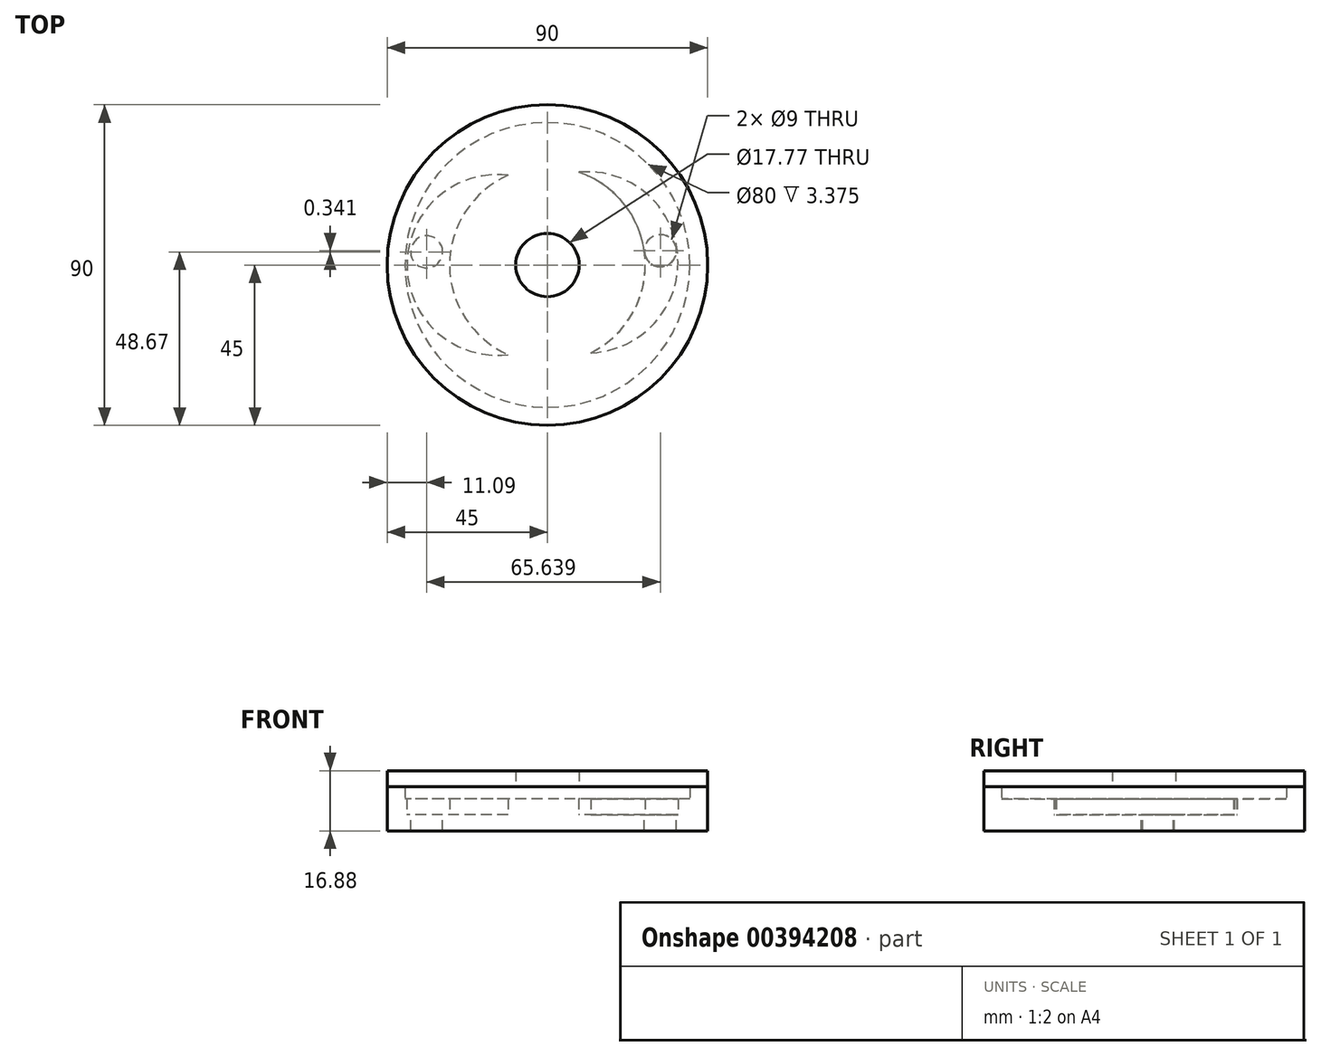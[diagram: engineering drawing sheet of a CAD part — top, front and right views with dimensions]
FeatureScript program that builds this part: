
annotation { "Feature Type Name" : "Feature", "Feature Type Description" : "" }
export const myFeature = defineFeature(function(context is Context, id is Id, definition is map)
    precondition{}
    {
        {
            var Q0;
            Q0=qCreatedBy(makeId("Top.planeOp"),FACE);
            var sketch = newSketch(context, id + "F0", { "sketchPlane" : qUnion([Q0])});
            skCircle(sketch, "E0", {"center": v(0, 0) * mm, "radius": 40 * mm});
            skCircle(sketch, "E1", {"center": v(0, 0) * mm, "radius": 45 * mm});
            skCircle(sketch, "E2", {"center": v(0, 0) * mm, "radius": 5 * mm});
            skSolve(sketch);
        }
        {
            var Q0;
            Q0=makeQuery(id+"F0.imprint","IMPRINT",FACE,{"disambiguationData":[TD([[makeQuery(id+"F0.imprint","IMPRINT",EDGE,{"derivedFrom":sQuery(id+"F0.wireOp",EDGE,"E0")}),1.0]])]});
            var Q1;
            Q1=makeQuery(id+"F0.imprint","IMPRINT",FACE,{"disambiguationData":[TD([[makeQuery(id+"F0.imprint","IMPRINT",EDGE,{"derivedFrom":sQuery(id+"F0.wireOp",EDGE,"E2")}),1.0]])]});
            extrude(context, id + "F1", {"entities" : qUnion([Q0, Q1]), "depth" : (2 * 9 / 4) * mm});
        }
        {
            var Q0;
            Q0=makeQuery(id+"F0.imprint","IMPRINT",FACE,{"disambiguationData":[TD([[makeQuery(id+"F0.imprint","IMPRINT",EDGE,{"derivedFrom":sQuery(id+"F0.wireOp",EDGE,"E0")}),-1.0]])]});
            extrude(context, id + "F2", {"entities" : qUnion([Q0]), "operationType" : NewBodyOperationType.ADD, "depth" : (3.5 * 9 / 4) * mm});
        }
        {
            var Q0;
            Q0=qCreatedBy(makeId("Top.planeOp"),FACE);
            var sketch = newSketch(context, id + "F3", { "sketchPlane" : qUnion([Q0])});
            skCircle(sketch, "E3", {"center": v(0, 0) * mm, "radius": 27.48 * mm});
            skCircle(sketch, "E4", {"center": v(-14.08, 0) * mm, "radius": 25.35 * mm});
            skCircle(sketch, "E5", {"center": v(11.25, 0.76) * mm, "radius": 25.4 * mm});
            skSolve(sketch);
        }
        {
            var Q0;
            {var subQ0=sQuery(id+"F3.wireOp",EDGE,"E5");var subQ1=sQuery(id+"F3.wireOp",EDGE,"E3");var subQ2=makeQuery(id+"F3.imprint","INTERSECT",VERTEX,{"disambiguationData":[OD(0.0)],"derivedFrom":[subQ1,subQ0]});Q0=makeQuery(id+"F3.imprint","IMPRINT",FACE,{"disambiguationData":[TD([[makeQuery(id+"F3.imprint","IMPRINT",EDGE,{"disambiguationData":[TD([[subQ2,1.0]])],"derivedFrom":subQ1}),-1.0]])]});}
            var Q1;
            {var subQ0=sQuery(id+"F3.wireOp",EDGE,"E4");var subQ1=sQuery(id+"F3.wireOp",EDGE,"E3");var subQ2=makeQuery(id+"F3.imprint","INTERSECT",VERTEX,{"disambiguationData":[OD(0.0)],"derivedFrom":[subQ1,subQ0]});Q1=makeQuery(id+"F3.imprint","IMPRINT",FACE,{"disambiguationData":[TD([[makeQuery(id+"F3.imprint","IMPRINT",EDGE,{"disambiguationData":[TD([[subQ2,-1.0]])],"derivedFrom":subQ1}),-1.0]])]});}
            var Q2;
            Q2=sQuery(id+"FPR7zcq1sT2BLRO_1.wireOp",EDGE,"gdkzTtUh-GniQ-s6fz-oA94-rAv7j2Bywu3O");
            extrude(context, id + "F4", {"entities" : qUnion([Q0, Q1]), "operationType" : NewBodyOperationType.REMOVE, "surfaceEntities" : qUnion([Q2]), "depth" : (2.5 * 9 / 4) * mm});
        }
        {
            var Q0;
            Q0=qCreatedBy(makeId("Top.planeOp"),FACE);
            var sketch = newSketch(context, id + "F5", { "sketchPlane" : qUnion([Q0])});
            skCircle(sketch, "E6", {"center": v(0, 0) * mm, "radius": 45 * mm});
            skCircle(sketch, "E7", {"center": v(-33.91, 3.67) * mm, "radius": 4.5 * mm});
            skCircle(sketch, "E8", {"center": v(31.73, 4.01) * mm, "radius": 4.5 * mm});
            skSolve(sketch);
        }
        {
            var Q0;
            Q0=makeQuery(id+"F5.imprint","IMPRINT",FACE,{"disambiguationData":[TD([[makeQuery(id+"F5.imprint","IMPRINT",EDGE,{"derivedFrom":sQuery(id+"F5.wireOp",EDGE,"E6")}),1.0]])]});
            extrude(context, id + "F6", {"entities" : qUnion([Q0]), "operationType" : NewBodyOperationType.ADD, "oppositeDirection" : true, "depth" : (2 * 9 / 4) * mm});
        }
        {
            var Q0;
            Q0=makeQuery(id+"F2.opExtrude","CAP_FACE",FACE,{"disambiguationData":[OSD([sQuery(id+"F0.wireOp",EDGE,"E0"),sQuery(id+"F0.wireOp",EDGE,"E1")])],"isStart":false});
            cPlane(context, id + "F7", {"entities" : qUnion([Q0]), "cplaneType" : CPlaneType.OFFSET, "offset" : 0 * mm, "width" : 150 * mm, "height" : 150 * mm});
        }
        {
            var Q0;
            Q0=qCreatedBy(id+"F7.planeOp",FACE);
            var sketch = newSketch(context, id + "F8", { "sketchPlane" : qUnion([Q0])});
            skCircle(sketch, "E9", {"center": v(0, 0) * mm, "radius": 45 * mm});
            skCircle(sketch, "E10", {"center": v(0, 0) * mm, "radius": 8.89 * mm});
            skSolve(sketch);
        }
        {
            var Q0;
            Q0=makeQuery(id+"F8.imprint","IMPRINT",FACE,{"disambiguationData":[TD([[makeQuery(id+"F8.imprint","IMPRINT",EDGE,{"derivedFrom":sQuery(id+"F8.wireOp",EDGE,"E9")}),1.0]])]});
            extrude(context, id + "F9", {"entities" : qUnion([Q0]), "depth" : (2 * 9 / 4) * mm});
        }
    });
